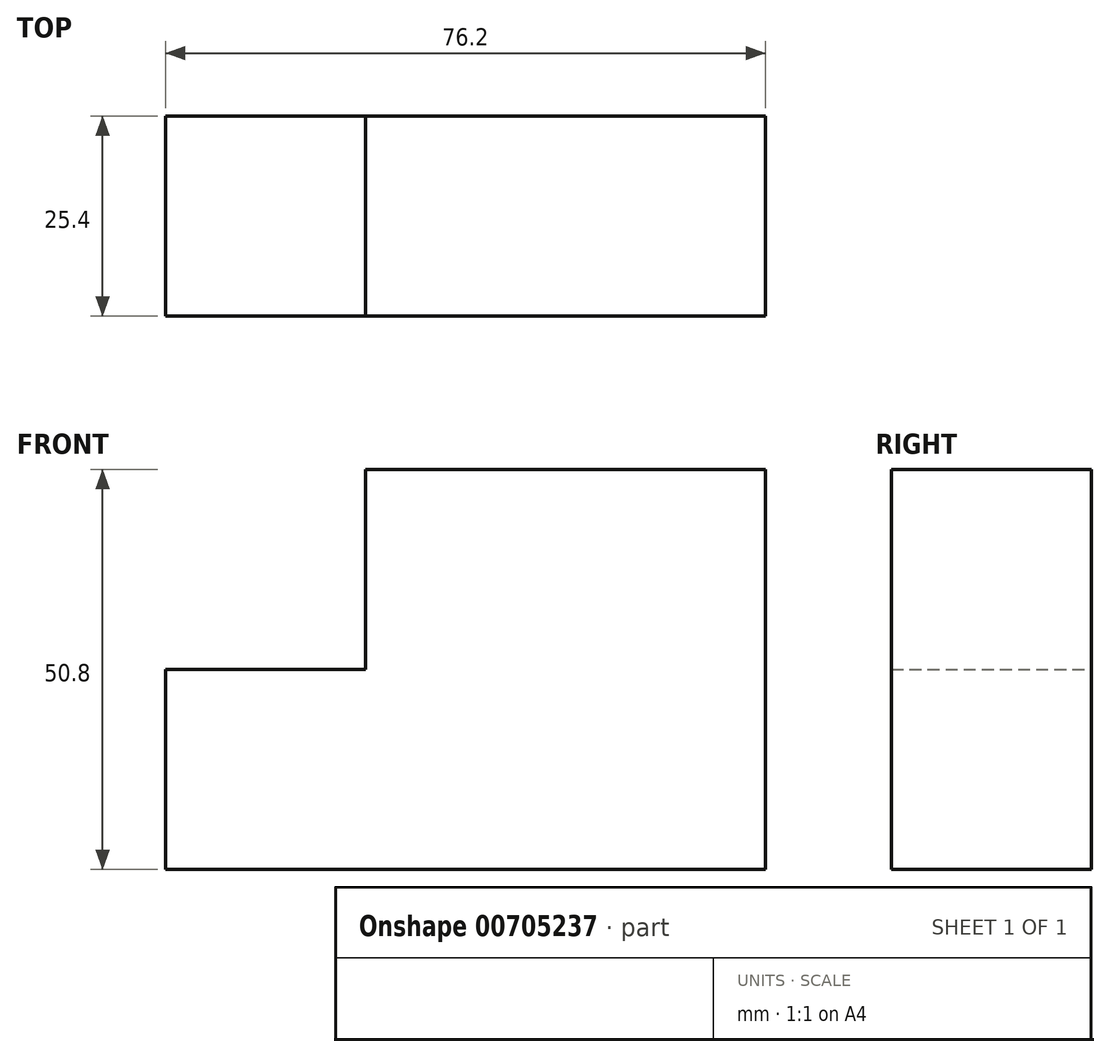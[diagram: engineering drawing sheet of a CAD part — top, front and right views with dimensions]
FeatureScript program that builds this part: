
annotation { "Feature Type Name" : "Feature", "Feature Type Description" : "" }
export const myFeature = defineFeature(function(context is Context, id is Id, definition is map)
    precondition{}
    {
        {
            var Q0;
            Q0=qCreatedBy(makeId("Front.planeOp"),FACE);
            var sketch = newSketch(context, id + "F0", { "sketchPlane" : qUnion([Q0])});
            skLineSegment(sketch, "E0.bottom", {"start": v(0, 0) * mm, "end": v(25.4, 0) * mm});
            skLineSegment(sketch, "E0.top", {"start": v(0, 25.4) * mm, "end": v(25.4, 25.4) * mm});
            skLineSegment(sketch, "E0.left", {"start": v(0, 0) * mm, "end": v(0, 25.4) * mm});
            skLineSegment(sketch, "E0.right", {"start": v(25.4, 0) * mm, "end": v(25.4, 25.4) * mm});
            skLineSegment(sketch, "E1.bottom", {"start": v(25.4, 25.4) * mm, "end": v(50.8, 25.4) * mm});
            skLineSegment(sketch, "E1.top", {"start": v(25.4, 0) * mm, "end": v(50.8, 0) * mm});
            skLineSegment(sketch, "E1.left", {"start": v(25.4, 25.4) * mm, "end": v(25.4, 0) * mm});
            skLineSegment(sketch, "E1.right", {"start": v(50.8, 25.4) * mm, "end": v(50.8, 0) * mm});
            skLineSegment(sketch, "E2.bottom", {"start": v(0, 25.4) * mm, "end": v(-25.4, 25.4) * mm});
            skLineSegment(sketch, "E2.top", {"start": v(0, 0) * mm, "end": v(-25.4, 0) * mm});
            skLineSegment(sketch, "E2.left", {"start": v(0, 25.4) * mm, "end": v(0, 0) * mm});
            skLineSegment(sketch, "E2.right", {"start": v(-25.4, 25.4) * mm, "end": v(-25.4, 0) * mm});
            skLineSegment(sketch, "E3.bottom", {"start": v(-25.4, 25.4) * mm, "end": v(0, 25.4) * mm});
            skLineSegment(sketch, "E3.top", {"start": v(-25.4, 50.8) * mm, "end": v(0, 50.8) * mm});
            skLineSegment(sketch, "E3.left", {"start": v(-25.4, 25.4) * mm, "end": v(-25.4, 50.8) * mm});
            skLineSegment(sketch, "E3.right", {"start": v(0, 25.4) * mm, "end": v(0, 50.8) * mm});
            skLineSegment(sketch, "E4.bottom", {"start": v(0, 50.8) * mm, "end": v(25.4, 50.8) * mm});
            skLineSegment(sketch, "E4.left", {"start": v(0, 50.8) * mm, "end": v(0, 25.4) * mm});
            skLineSegment(sketch, "E4.right", {"start": v(25.4, 50.8) * mm, "end": v(25.4, 25.4) * mm});
            skLineSegment(sketch, "E5.bottom", {"start": v(25.4, 50.8) * mm, "end": v(50.8, 50.8) * mm});
            skLineSegment(sketch, "E5.right", {"start": v(50.8, 50.8) * mm, "end": v(50.8, 25.4) * mm});
            skSolve(sketch);
        }
        {
            var Q0;
            Q0=makeQuery(id+"F0.imprint","IMPRINT",FACE,{"disambiguationData":[TD([[makeQuery(id+"F0.imprint","IMPRINT",EDGE,{"derivedFrom":sQuery(id+"F0.wireOp",EDGE,"E3.bottom")}),1.0]])]});
            var Q1;
            Q1=makeQuery(id+"F0.imprint","IMPRINT",FACE,{"disambiguationData":[TD([[makeQuery(id+"F0.imprint","IMPRINT",EDGE,{"derivedFrom":sQuery(id+"F0.wireOp",EDGE,"E2.top")}),-1.0]])]});
            var Q2;
            Q2=makeQuery(id+"F0.imprint","IMPRINT",FACE,{"disambiguationData":[TD([[makeQuery(id+"F0.imprint","IMPRINT",EDGE,{"derivedFrom":sQuery(id+"F0.wireOp",EDGE,"E4.bottom")}),-1.0]])]});
            var Q3;
            Q3=makeQuery(id+"F0.imprint","IMPRINT",FACE,{"disambiguationData":[TD([[makeQuery(id+"F0.imprint","IMPRINT",EDGE,{"derivedFrom":sQuery(id+"F0.wireOp",EDGE,"E0.bottom")}),1.0]])]});
            var Q4;
            Q4=makeQuery(id+"F0.imprint","IMPRINT",FACE,{"disambiguationData":[TD([[makeQuery(id+"F0.imprint","IMPRINT",EDGE,{"derivedFrom":sQuery(id+"F0.wireOp",EDGE,"E5.bottom")}),-1.0]])]});
            var Q5;
            Q5=makeQuery(id+"F0.imprint","IMPRINT",FACE,{"disambiguationData":[TD([[makeQuery(id+"F0.imprint","IMPRINT",EDGE,{"derivedFrom":sQuery(id+"F0.wireOp",EDGE,"E1.top")}),1.0]])]});
            extrude(context, id + "F1", {"entities" : qUnion([Q0, Q1, Q2, Q3, Q4, Q5]), "depth" : 25.4 * mm, "offsetDistance" : 25.4 * mm});
        }
    });
